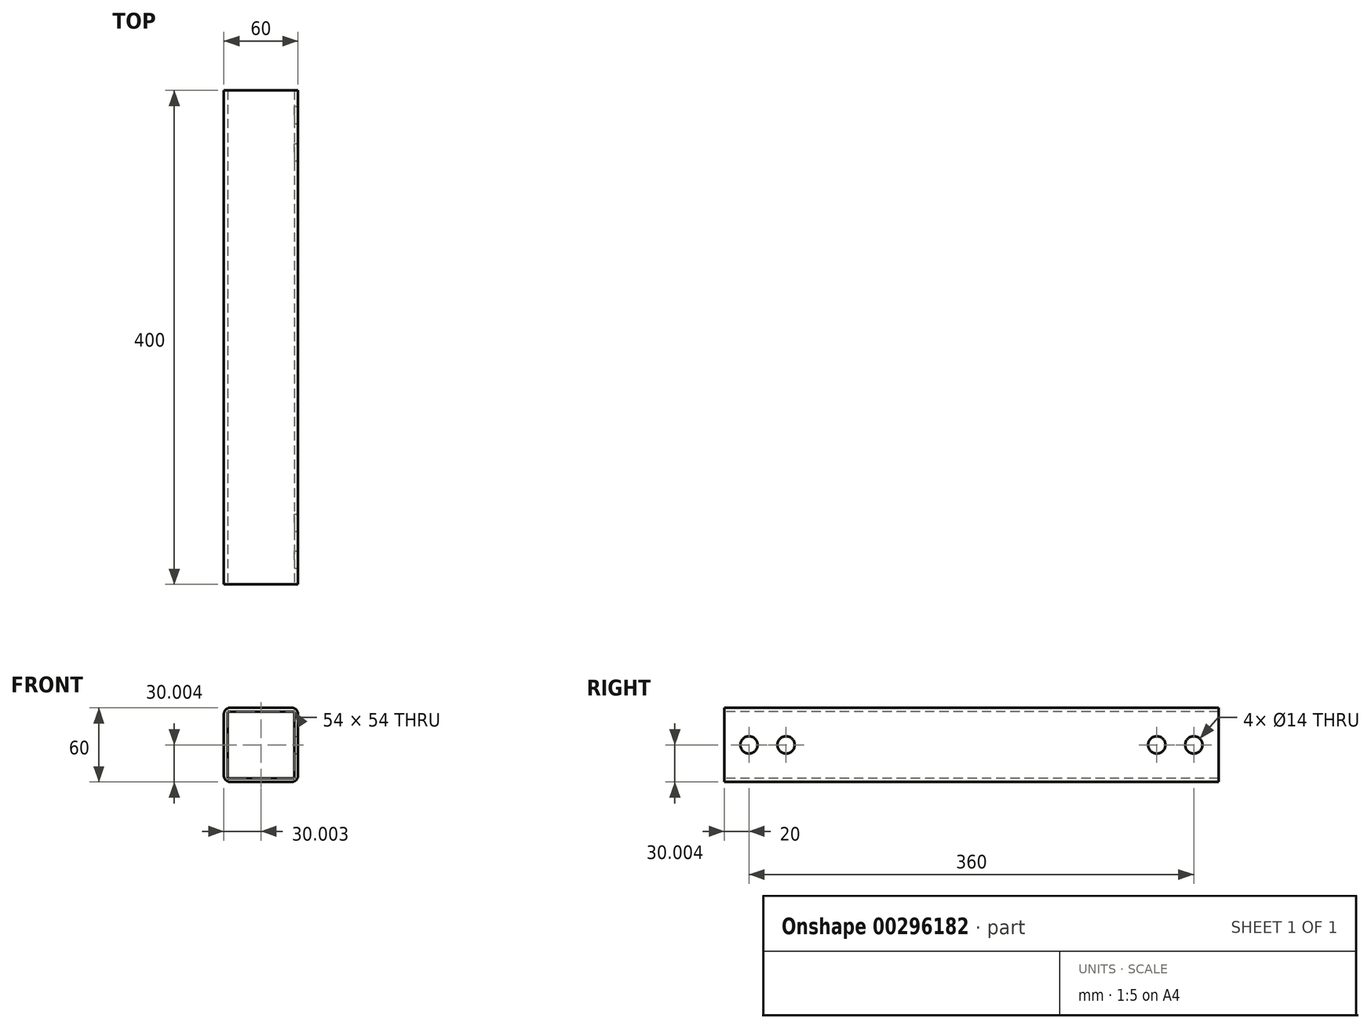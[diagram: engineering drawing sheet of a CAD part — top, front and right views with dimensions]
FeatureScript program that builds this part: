
annotation { "Feature Type Name" : "Feature", "Feature Type Description" : "" }
export const myFeature = defineFeature(function(context is Context, id is Id, definition is map)
    precondition{}
    {
        {
            var Q0;
            Q0=qCreatedBy(makeId("Front.planeOp"),FACE);
            var sketch = newSketch(context, id + "F0", { "sketchPlane" : qUnion([Q0])});
            skLineSegment(sketch, "E0.bottom", {"start": v(-33.99, -56) * mm, "end": v(-83.99, -56) * mm});
            skLineSegment(sketch, "E0.top", {"start": v(-33.99, -116) * mm, "end": v(-83.99, -116) * mm});
            skLineSegment(sketch, "E0.left", {"start": v(-28.99, -61) * mm, "end": v(-28.99, -111) * mm});
            skLineSegment(sketch, "E0.right", {"start": v(-88.99, -61) * mm, "end": v(-88.99, -111) * mm});
            skPoint(sketch, "E0.middle", {"position": v(-58.99, -86) * mm});
            skPoint(sketch, "E1.visualSharp", {"position": v(-88.99, -56) * mm});
            skArc(sketch, "E1.filletArc", {"start": v(-83.99, -56) * mm, "mid": v(-87.52, -57.46) * mm, "end": v(-88.99, -61) * mm});
            skPoint(sketch, "E2.visualSharp", {"position": v(-28.99, -56) * mm});
            skArc(sketch, "E2.filletArc", {"start": v(-28.99, -61) * mm, "mid": v(-30.45, -57.46) * mm, "end": v(-33.99, -56) * mm});
            skPoint(sketch, "E3.visualSharp", {"position": v(-28.99, -116) * mm});
            skArc(sketch, "E3.filletArc", {"start": v(-33.99, -116) * mm, "mid": v(-30.45, -114.53) * mm, "end": v(-28.99, -111) * mm});
            skPoint(sketch, "E4.visualSharp", {"position": v(-88.99, -116) * mm});
            skArc(sketch, "E4.filletArc", {"start": v(-88.99, -111) * mm, "mid": v(-87.52, -114.53) * mm, "end": v(-83.99, -116) * mm});
            skLineSegment(sketch, "E5.0", {"start": v(-31.99, -113) * mm, "end": v(-85.99, -113) * mm});
            skLineSegment(sketch, "E5.1", {"start": v(-31.99, -59) * mm, "end": v(-31.99, -113) * mm});
            skLineSegment(sketch, "E5.2", {"start": v(-31.99, -59) * mm, "end": v(-85.99, -59) * mm});
            skLineSegment(sketch, "E5.3", {"start": v(-85.99, -59) * mm, "end": v(-85.99, -113) * mm});
            skSolve(sketch);
        }
        {
            var Q0;
            Q0=makeQuery(id+"F0.imprint","IMPRINT",FACE,{"disambiguationData":[TD([[makeQuery(id+"F0.imprint","IMPRINT",EDGE,{"derivedFrom":sQuery(id+"F0.wireOp",EDGE,"WBqOBU3J-LVuc-RZdo-IQ9V-Ewm5Q1t9rkOa.bottom")}),1.0]])]});
            var Q1;
            Q1=makeQuery(id+"F0.imprint","IMPRINT",FACE,{"disambiguationData":[TD([[makeQuery(id+"F0.imprint","IMPRINT",EDGE,{"derivedFrom":sQuery(id+"F0.wireOp",EDGE,"99b7a4c1-c7c6-4472-a640-d268f497dcd0.bottom")}),1.0]])]});
            var Q2;
            Q2=makeQuery(id+"F0.imprint","IMPRINT",FACE,{"disambiguationData":[TD([[makeQuery(id+"F0.imprint","IMPRINT",EDGE,{"derivedFrom":sQuery(id+"F0.wireOp",EDGE,"E0.bottom")}),1.0]])]});
            extrude(context, id + "F1", {"entities" : qUnion([Q0, Q1, Q2]), "oppositeDirection" : true, "depth" : 400 * mm});
        }
        {
            var Q0;
            Q0=makeQuery(id+"F1.opExtrude","SWEPT_FACE",FACE,{"disambiguationData":[OSD([sQuery(id+"F0.wireOp",EDGE,"E0.left")])]});
            var sketch = newSketch(context, id + "F2", { "sketchPlane" : qUnion([Q0])});
            skLineSegment(sketch, "E6", {"start": v(0, -86) * mm, "end": v(400, -86) * mm, "construction": true});
            skCircle(sketch, "E7", {"center": v(20, -86) * mm, "radius": 7 * mm});
            skCircle(sketch, "E8", {"center": v(50, -86) * mm, "radius": 7 * mm});
            skCircle(sketch, "E9", {"center": v(350, -86) * mm, "radius": 7 * mm});
            skCircle(sketch, "E10", {"center": v(380, -86) * mm, "radius": 7 * mm});
            skSolve(sketch);
        }
        {
            var Q0;
            Q0=makeQuery(id+"F2.imprint","IMPRINT",FACE,{"disambiguationData":[TD([[makeQuery(id+"F2.imprint","IMPRINT",EDGE,{"derivedFrom":sQuery(id+"F2.wireOp",EDGE,"E7")}),1.0]])]});
            var Q1;
            Q1=makeQuery(id+"F2.imprint","IMPRINT",FACE,{"disambiguationData":[TD([[makeQuery(id+"F2.imprint","IMPRINT",EDGE,{"derivedFrom":sQuery(id+"F2.wireOp",EDGE,"E8")}),1.0]])]});
            var Q2;
            Q2=makeQuery(id+"F2.imprint","IMPRINT",FACE,{"disambiguationData":[TD([[makeQuery(id+"F2.imprint","IMPRINT",EDGE,{"derivedFrom":sQuery(id+"F2.wireOp",EDGE,"E9")}),1.0]])]});
            var Q3;
            Q3=makeQuery(id+"F2.imprint","IMPRINT",FACE,{"disambiguationData":[TD([[makeQuery(id+"F2.imprint","IMPRINT",EDGE,{"derivedFrom":sQuery(id+"F2.wireOp",EDGE,"E10")}),1.0]])]});
            extrude(context, id + "F3", {"entities" : qUnion([Q0, Q1, Q2, Q3]), "operationType" : NewBodyOperationType.REMOVE, "endBound" : BoundingType.UP_TO_NEXT, "oppositeDirection" : true, "depth" : 25 * mm});
        }
    });
